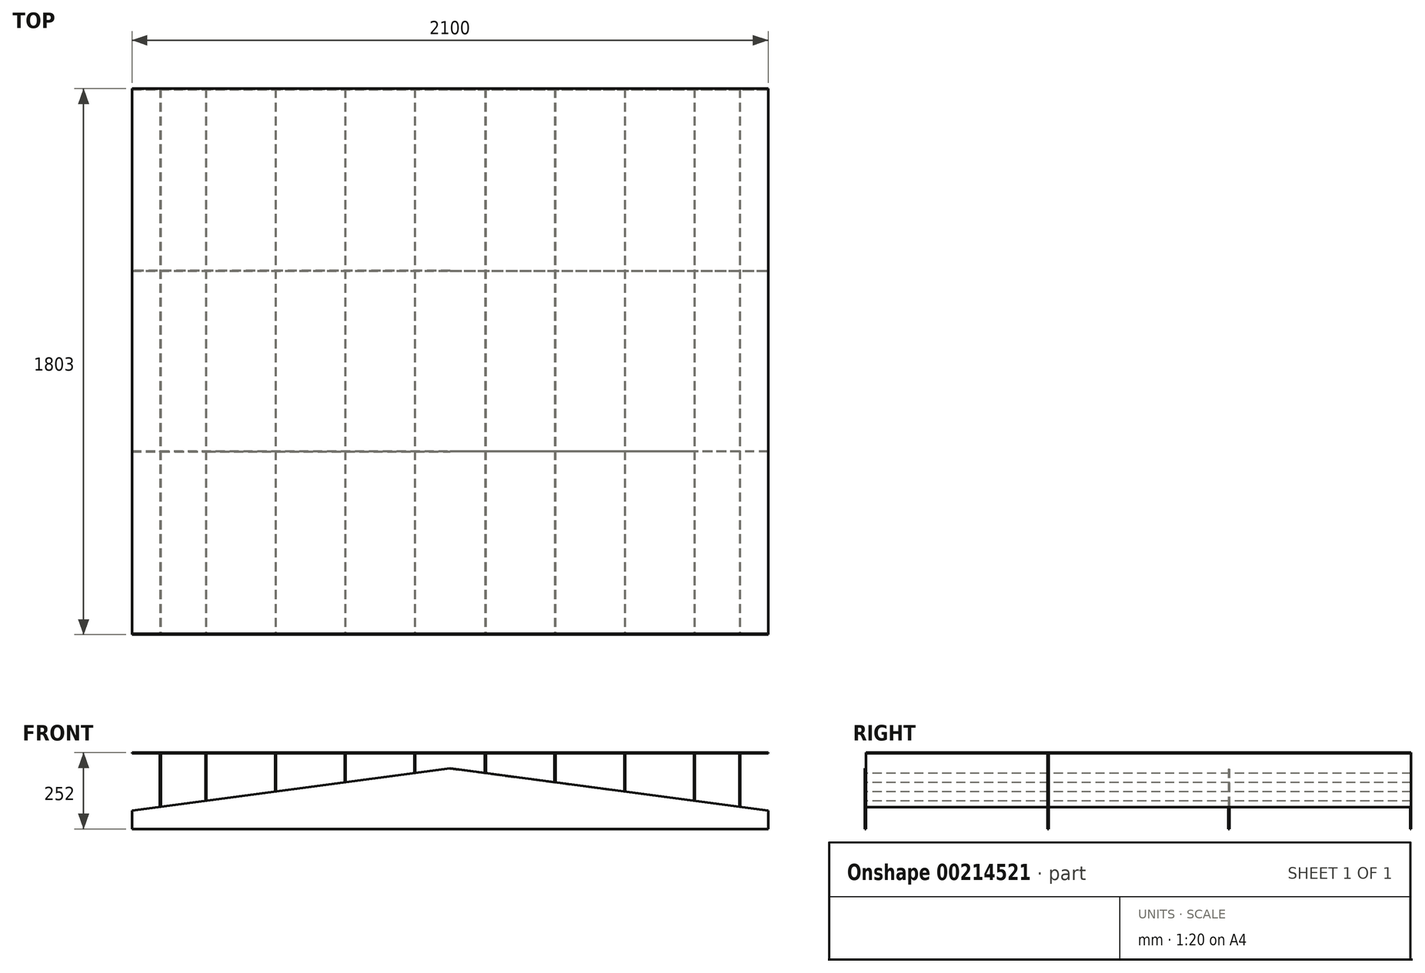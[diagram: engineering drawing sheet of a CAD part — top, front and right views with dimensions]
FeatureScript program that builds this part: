
annotation { "Feature Type Name" : "Feature", "Feature Type Description" : "" }
export const myFeature = defineFeature(function(context is Context, id is Id, definition is map)
    precondition{}
    {
        {
            var Q0;
            Q0=qCreatedBy(makeId("Front.planeOp"),FACE);
            var sketch = newSketch(context, id + "F0", { "sketchPlane" : qUnion([Q0])});
            skLineSegment(sketch, "E0", {"start": v(0, -314.94) * mm, "end": v(-1050, -314.94) * mm});
            skLineSegment(sketch, "E1", {"start": v(-1050, -314.94) * mm, "end": v(-1050, -254.94) * mm});
            skLineSegment(sketch, "E2", {"start": v(-1050, -254.94) * mm, "end": v(0, -114.94) * mm});
            skLineSegment(sketch, "E3", {"start": v(0, -64.94) * mm, "end": v(-1050, -64.94) * mm, "construction": true});
            skLineSegment(sketch, "E4.bottom", {"start": v(-118, -64.94) * mm, "end": v(-115, -64.94) * mm});
            skLineSegment(sketch, "E4.top", {"start": v(-118, -130.67) * mm, "end": v(-115, -130.27) * mm});
            skLineSegment(sketch, "E4.left", {"start": v(-118, -64.94) * mm, "end": v(-118, -130.67) * mm});
            skLineSegment(sketch, "E4.right", {"start": v(-115, -64.94) * mm, "end": v(-115, -130.27) * mm});
            skLineSegment(sketch, "E5.bottom", {"start": v(-348, -64.94) * mm, "end": v(-345, -64.94) * mm});
            skLineSegment(sketch, "E5.top", {"start": v(-348, -161.34) * mm, "end": v(-345, -160.94) * mm});
            skLineSegment(sketch, "E5.left", {"start": v(-348, -64.94) * mm, "end": v(-348, -161.34) * mm});
            skLineSegment(sketch, "E5.right", {"start": v(-345, -64.94) * mm, "end": v(-345, -160.94) * mm});
            skLineSegment(sketch, "E6.bottom", {"start": v(-578, -64.94) * mm, "end": v(-575, -64.94) * mm});
            skLineSegment(sketch, "E6.top", {"start": v(-578, -192) * mm, "end": v(-575, -191.6) * mm});
            skLineSegment(sketch, "E6.left", {"start": v(-578, -64.94) * mm, "end": v(-578, -192) * mm});
            skLineSegment(sketch, "E6.right", {"start": v(-575, -64.94) * mm, "end": v(-575, -191.6) * mm});
            skLineSegment(sketch, "E7.bottom", {"start": v(-808, -64.94) * mm, "end": v(-805, -64.94) * mm});
            skLineSegment(sketch, "E7.top", {"start": v(-808, -222.67) * mm, "end": v(-805, -222.27) * mm});
            skLineSegment(sketch, "E7.left", {"start": v(-808, -64.94) * mm, "end": v(-808, -222.67) * mm});
            skLineSegment(sketch, "E7.right", {"start": v(-805, -64.94) * mm, "end": v(-805, -222.27) * mm});
            skLineSegment(sketch, "E8.bottom", {"start": v(-958, -64.94) * mm, "end": v(-955, -64.94) * mm});
            skLineSegment(sketch, "E8.top", {"start": v(-958, -242.67) * mm, "end": v(-955, -242.27) * mm});
            skLineSegment(sketch, "E8.left", {"start": v(-958, -64.94) * mm, "end": v(-958, -242.67) * mm});
            skLineSegment(sketch, "E8.right", {"start": v(-955, -64.94) * mm, "end": v(-955, -242.27) * mm});
            skLineSegment(sketch, "E9.MirrorCS", {"start": v(578, -192) * mm, "end": v(575, -191.6) * mm});
            skLineSegment(sketch, "E10.MirrorCS", {"start": v(958, -242.67) * mm, "end": v(955, -242.27) * mm});
            skLineSegment(sketch, "E11.MirrorCS", {"start": v(578, -64.94) * mm, "end": v(575, -64.94) * mm});
            skLineSegment(sketch, "E12.MirrorCS", {"start": v(348, -161.34) * mm, "end": v(345, -160.94) * mm});
            skLineSegment(sketch, "E13.MirrorCS", {"start": v(808, -222.67) * mm, "end": v(805, -222.27) * mm});
            skLineSegment(sketch, "E14.MirrorCS", {"start": v(348, -64.94) * mm, "end": v(345, -64.94) * mm});
            skLineSegment(sketch, "E15.MirrorCS", {"start": v(958, -64.94) * mm, "end": v(955, -64.94) * mm});
            skLineSegment(sketch, "E16.MirrorCS", {"start": v(808, -64.94) * mm, "end": v(805, -64.94) * mm});
            skLineSegment(sketch, "E17.MirrorCS", {"start": v(118, -64.94) * mm, "end": v(115, -64.94) * mm});
            skLineSegment(sketch, "E18.MirrorCS", {"start": v(118, -130.67) * mm, "end": v(115, -130.27) * mm});
            skLineSegment(sketch, "E19.MirrorCS", {"start": v(575, -64.94) * mm, "end": v(575, -191.6) * mm});
            skLineSegment(sketch, "E20.MirrorCS", {"start": v(118, -64.94) * mm, "end": v(118, -130.67) * mm});
            skLineSegment(sketch, "E21.MirrorCS", {"start": v(1050, -314.94) * mm, "end": v(1050, -254.94) * mm});
            skLineSegment(sketch, "E22.MirrorCS", {"start": v(115, -64.94) * mm, "end": v(115, -130.27) * mm});
            skLineSegment(sketch, "E23.MirrorCS", {"start": v(955, -64.94) * mm, "end": v(955, -242.27) * mm});
            skLineSegment(sketch, "E24.MirrorCS", {"start": v(805, -64.94) * mm, "end": v(805, -222.27) * mm});
            skLineSegment(sketch, "E25.MirrorCS", {"start": v(348, -64.94) * mm, "end": v(348, -161.34) * mm});
            skLineSegment(sketch, "E26.MirrorCS", {"start": v(578, -64.94) * mm, "end": v(578, -192) * mm});
            skLineSegment(sketch, "E27.MirrorCS", {"start": v(958, -64.94) * mm, "end": v(958, -242.67) * mm});
            skLineSegment(sketch, "E28.MirrorCS", {"start": v(345, -64.94) * mm, "end": v(345, -160.94) * mm});
            skLineSegment(sketch, "E29.MirrorCS", {"start": v(1050, -254.94) * mm, "end": v(0, -114.94) * mm});
            skLineSegment(sketch, "E30.MirrorCS", {"start": v(0, -314.94) * mm, "end": v(1050, -314.94) * mm});
            skLineSegment(sketch, "E31.MirrorCS", {"start": v(808, -64.94) * mm, "end": v(808, -222.67) * mm});
            skLineSegment(sketch, "E32.MirrorCS", {"start": v(0, -64.94) * mm, "end": v(1050, -64.94) * mm, "construction": true});
            skSolve(sketch);
        }
        {
            var Q0;
            Q0 = qSketchRegion(id + "F0", true);
            extrude(context, id + "F1", {"entities" : qUnion([Q0]), "depth" : 3 * mm, "offsetDistance" : 25 * mm});
        }
        {
            var Q0;
            Q0=makeQuery(id+"F1.opExtrude","CAP_FACE",FACE,{"disambiguationData":[OSD([sQuery(id+"F0.wireOp",EDGE,"E0"),sQuery(id+"F0.wireOp",EDGE,"E1"),sQuery(id+"F0.wireOp",EDGE,"E2"),sQuery(id+"F0.wireOp",EDGE,"E4.bottom"),sQuery(id+"F0.wireOp",EDGE,"E4.left"),sQuery(id+"F0.wireOp",EDGE,"E4.right"),sQuery(id+"F0.wireOp",EDGE,"E5.bottom"),sQuery(id+"F0.wireOp",EDGE,"E5.left"),sQuery(id+"F0.wireOp",EDGE,"E5.right"),sQuery(id+"F0.wireOp",EDGE,"E6.bottom"),sQuery(id+"F0.wireOp",EDGE,"E6.left"),sQuery(id+"F0.wireOp",EDGE,"E6.right"),sQuery(id+"F0.wireOp",EDGE,"E7.bottom"),sQuery(id+"F0.wireOp",EDGE,"E7.left"),sQuery(id+"F0.wireOp",EDGE,"E7.right"),sQuery(id+"F0.wireOp",EDGE,"E8.bottom"),sQuery(id+"F0.wireOp",EDGE,"E8.left"),sQuery(id+"F0.wireOp",EDGE,"E8.right"),sQuery(id+"F0.wireOp",EDGE,"E11.MirrorCS"),sQuery(id+"F0.wireOp",EDGE,"E14.MirrorCS"),sQuery(id+"F0.wireOp",EDGE,"E15.MirrorCS"),sQuery(id+"F0.wireOp",EDGE,"E16.MirrorCS"),sQuery(id+"F0.wireOp",EDGE,"E17.MirrorCS"),sQuery(id+"F0.wireOp",EDGE,"E19.MirrorCS"),sQuery(id+"F0.wireOp",EDGE,"E20.MirrorCS"),sQuery(id+"F0.wireOp",EDGE,"E21.MirrorCS"),sQuery(id+"F0.wireOp",EDGE,"E22.MirrorCS"),sQuery(id+"F0.wireOp",EDGE,"E23.MirrorCS"),sQuery(id+"F0.wireOp",EDGE,"E24.MirrorCS"),sQuery(id+"F0.wireOp",EDGE,"E25.MirrorCS"),sQuery(id+"F0.wireOp",EDGE,"E26.MirrorCS"),sQuery(id+"F0.wireOp",EDGE,"E27.MirrorCS"),sQuery(id+"F0.wireOp",EDGE,"E28.MirrorCS"),sQuery(id+"F0.wireOp",EDGE,"E29.MirrorCS"),sQuery(id+"F0.wireOp",EDGE,"E30.MirrorCS"),sQuery(id+"F0.wireOp",EDGE,"E31.MirrorCS")])],"isStart":false});
            cPlane(context, id + "F2", {"entities" : qUnion([Q0]), "cplaneType" : CPlaneType.OFFSET, "offset" : 600 * mm, "width" : 150 * mm, "height" : 150 * mm});
        }
        {
            var Q0;
            Q0=qCreatedBy(id+"F2.planeOp",FACE);
            var sketch = newSketch(context, id + "F3", { "sketchPlane" : qUnion([Q0])});
            skLineSegment(sketch, "E33.bottom", {"start": v(-958, -64.94) * mm, "end": v(-955, -64.94) * mm});
            skLineSegment(sketch, "E33.top", {"start": v(-958, -242.67) * mm, "end": v(-955, -242.67) * mm});
            skLineSegment(sketch, "E33.left", {"start": v(-958, -64.94) * mm, "end": v(-958, -242.67) * mm});
            skLineSegment(sketch, "E33.right", {"start": v(-955, -64.94) * mm, "end": v(-955, -242.67) * mm});
            skLineSegment(sketch, "E34.bottom", {"start": v(-808, -64.94) * mm, "end": v(-805, -64.94) * mm});
            skLineSegment(sketch, "E34.top", {"start": v(-808, -222.67) * mm, "end": v(-805, -222.67) * mm});
            skLineSegment(sketch, "E34.left", {"start": v(-808, -64.94) * mm, "end": v(-808, -222.67) * mm});
            skLineSegment(sketch, "E34.right", {"start": v(-805, -64.94) * mm, "end": v(-805, -222.67) * mm});
            skLineSegment(sketch, "E35.bottom", {"start": v(-578, -64.94) * mm, "end": v(-575, -64.94) * mm});
            skLineSegment(sketch, "E35.top", {"start": v(-578, -192) * mm, "end": v(-575, -192) * mm});
            skLineSegment(sketch, "E35.left", {"start": v(-578, -64.94) * mm, "end": v(-578, -192) * mm});
            skLineSegment(sketch, "E35.right", {"start": v(-575, -64.94) * mm, "end": v(-575, -192) * mm});
            skLineSegment(sketch, "E36.bottom", {"start": v(-348, -64.94) * mm, "end": v(-345, -64.94) * mm});
            skLineSegment(sketch, "E36.top", {"start": v(-348, -161.34) * mm, "end": v(-345, -161.34) * mm});
            skLineSegment(sketch, "E36.left", {"start": v(-348, -64.94) * mm, "end": v(-348, -161.34) * mm});
            skLineSegment(sketch, "E36.right", {"start": v(-345, -64.94) * mm, "end": v(-345, -161.34) * mm});
            skLineSegment(sketch, "E37.bottom", {"start": v(-118, -64.94) * mm, "end": v(-115, -64.94) * mm});
            skLineSegment(sketch, "E37.top", {"start": v(-118, -130.67) * mm, "end": v(-115, -130.67) * mm});
            skLineSegment(sketch, "E37.left", {"start": v(-118, -64.94) * mm, "end": v(-118, -130.67) * mm});
            skLineSegment(sketch, "E37.right", {"start": v(-115, -64.94) * mm, "end": v(-115, -130.67) * mm});
            skLineSegment(sketch, "E38.MirrorCS", {"start": v(348, -161.34) * mm, "end": v(345, -161.34) * mm});
            skLineSegment(sketch, "E39.MirrorCS", {"start": v(578, -64.94) * mm, "end": v(575, -64.94) * mm});
            skLineSegment(sketch, "E40.MirrorCS", {"start": v(808, -222.67) * mm, "end": v(805, -222.67) * mm});
            skLineSegment(sketch, "E41.MirrorCS", {"start": v(348, -64.94) * mm, "end": v(345, -64.94) * mm});
            skLineSegment(sketch, "E42.MirrorCS", {"start": v(118, -130.67) * mm, "end": v(115, -130.67) * mm});
            skLineSegment(sketch, "E43.MirrorCS", {"start": v(958, -64.94) * mm, "end": v(955, -64.94) * mm});
            skLineSegment(sketch, "E44.MirrorCS", {"start": v(115, -64.94) * mm, "end": v(115, -130.67) * mm});
            skLineSegment(sketch, "E45.MirrorCS", {"start": v(958, -242.67) * mm, "end": v(955, -242.67) * mm});
            skLineSegment(sketch, "E46.MirrorCS", {"start": v(118, -64.94) * mm, "end": v(118, -130.67) * mm});
            skLineSegment(sketch, "E47.MirrorCS", {"start": v(578, -192) * mm, "end": v(575, -192) * mm});
            skLineSegment(sketch, "E48.MirrorCS", {"start": v(808, -64.94) * mm, "end": v(805, -64.94) * mm});
            skLineSegment(sketch, "E49.MirrorCS", {"start": v(118, -64.94) * mm, "end": v(115, -64.94) * mm});
            skLineSegment(sketch, "E50.MirrorCS", {"start": v(575, -64.94) * mm, "end": v(575, -192) * mm});
            skLineSegment(sketch, "E51.MirrorCS", {"start": v(958, -64.94) * mm, "end": v(958, -242.67) * mm});
            skLineSegment(sketch, "E52.MirrorCS", {"start": v(348, -64.94) * mm, "end": v(348, -161.34) * mm});
            skLineSegment(sketch, "E53.MirrorCS", {"start": v(955, -64.94) * mm, "end": v(955, -242.67) * mm});
            skLineSegment(sketch, "E54.MirrorCS", {"start": v(805, -64.94) * mm, "end": v(805, -222.67) * mm});
            skLineSegment(sketch, "E55.MirrorCS", {"start": v(808, -64.94) * mm, "end": v(808, -222.67) * mm});
            skLineSegment(sketch, "E56.MirrorCS", {"start": v(345, -64.94) * mm, "end": v(345, -161.34) * mm});
            skLineSegment(sketch, "E57.MirrorCS", {"start": v(578, -64.94) * mm, "end": v(578, -192) * mm});
            skSolve(sketch);
        }
        {
            var Q0;
            Q0 = qSketchRegion(id + "F3", true);
            extrude(context, id + "F4", {"entities" : qUnion([Q0]), "oppositeDirection" : true, "depth" : 1800 * mm, "offsetDistance" : 25 * mm});
        }
        {
            var Q0;
            Q0=qCreatedBy(id+"F2.planeOp",FACE);
            cPlane(context, id + "F5", {"entities" : qUnion([Q0]), "cplaneType" : CPlaneType.OFFSET, "offset" : 1200 * mm, "oppositeDirection" : true, "width" : 150 * mm, "height" : 150 * mm});
        }
        {
            var Q0;
            Q0=qCreatedBy(id+"F5.planeOp",FACE);
            var sketch = newSketch(context, id + "F6", { "sketchPlane" : qUnion([Q0])});
            skLineSegment(sketch, "E58", {"start": v(0, -116.92) * mm, "end": v(-1050, -254.94) * mm});
            skLineSegment(sketch, "E59", {"start": v(-1050, -254.94) * mm, "end": v(-1050, -314.94) * mm});
            skLineSegment(sketch, "E60", {"start": v(-1050, -314.94) * mm, "end": v(0, -314.94) * mm});
            skLineSegment(sketch, "E61.MirrorCS", {"start": v(1050, -254.94) * mm, "end": v(1050, -314.94) * mm});
            skLineSegment(sketch, "E62.MirrorCS", {"start": v(0, -116.92) * mm, "end": v(1050, -254.94) * mm});
            skLineSegment(sketch, "E63.MirrorCS", {"start": v(1050, -314.94) * mm, "end": v(0, -314.94) * mm});
            skSolve(sketch);
        }
        {
            var Q0;
            Q0 = qSketchRegion(id + "F6", true);
            extrude(context, id + "F7", {"entities" : qUnion([Q0]), "depth" : 3 * mm, "offsetDistance" : 25 * mm});
        }
        {
            var Q0;
            Q0=qCreatedBy(id+"F5.planeOp",FACE);
            cPlane(context, id + "F8", {"entities" : qUnion([Q0]), "cplaneType" : CPlaneType.OFFSET, "offset" : 600 * mm, "oppositeDirection" : true, "width" : 150 * mm, "height" : 150 * mm});
        }
        {
            var Q0;
            Q0=qCreatedBy(id+"F8.planeOp",FACE);
            var sketch = newSketch(context, id + "F9", { "sketchPlane" : qUnion([Q0])});
            skLineSegment(sketch, "E64", {"start": v(0, -114.94) * mm, "end": v(-1050, -254.94) * mm});
            skLineSegment(sketch, "E65", {"start": v(-1050, -254.94) * mm, "end": v(-1050, -314.94) * mm});
            skLineSegment(sketch, "E66", {"start": v(-1050, -314.94) * mm, "end": v(0, -314.94) * mm});
            skLineSegment(sketch, "E67.MirrorCS", {"start": v(1050, -254.94) * mm, "end": v(1050, -314.94) * mm});
            skLineSegment(sketch, "E68.MirrorCS", {"start": v(1050, -314.94) * mm, "end": v(0, -314.94) * mm});
            skLineSegment(sketch, "E69.MirrorCS", {"start": v(0, -114.94) * mm, "end": v(1050, -254.94) * mm});
            skSolve(sketch);
        }
        {
            var Q0;
            Q0 = qSketchRegion(id + "F9", true);
            extrude(context, id + "F10", {"entities" : qUnion([Q0]), "depth" : 3 * mm, "offsetDistance" : 25 * mm});
        }
        {
            var Q0;
            Q0=makeQuery(id+"F4.opExtrude","SWEPT_FACE",FACE,{"disambiguationData":[OSD([sQuery(id+"F3.wireOp",EDGE,"E33.bottom")])]});
            var sketch = newSketch(context, id + "F11", { "sketchPlane" : qUnion([Q0])});
            skLineSegment(sketch, "E70.bottom", {"start": v(-1050, 1197) * mm, "end": v(1050, 1197) * mm});
            skLineSegment(sketch, "E70.top", {"start": v(-1050, -603) * mm, "end": v(1050, -603) * mm});
            skLineSegment(sketch, "E70.left", {"start": v(-1050, 1197) * mm, "end": v(-1050, -603) * mm});
            skLineSegment(sketch, "E70.right", {"start": v(1050, 1197) * mm, "end": v(1050, -603) * mm});
            skSolve(sketch);
        }
        {
            var Q0;
            Q0 = qSketchRegion(id + "F11", true);
            extrude(context, id + "F12", {"entities" : qUnion([Q0]), "depth" : 2 * mm, "offsetDistance" : 25 * mm});
        }
        {
            var Q0;
            Q0=qCreatedBy(id+"F2.planeOp",FACE);
            var sketch = newSketch(context, id + "F13", { "sketchPlane" : qUnion([Q0])});
            skLineSegment(sketch, "E71", {"start": v(0, -114.94) * mm, "end": v(-1050, -254.94) * mm});
            skLineSegment(sketch, "E72", {"start": v(-1050, -254.94) * mm, "end": v(-1050, -314.94) * mm});
            skLineSegment(sketch, "E73", {"start": v(-1050, -314.94) * mm, "end": v(0, -314.94) * mm});
            skLineSegment(sketch, "E74.MirrorCS", {"start": v(0, -114.94) * mm, "end": v(1050, -254.94) * mm});
            skLineSegment(sketch, "E75.MirrorCS", {"start": v(1050, -314.94) * mm, "end": v(0, -314.94) * mm});
            skLineSegment(sketch, "E76.MirrorCS", {"start": v(1050, -254.94) * mm, "end": v(1050, -314.94) * mm});
            skSolve(sketch);
        }
        {
            var Q0;
            Q0 = qSketchRegion(id + "F13", true);
            extrude(context, id + "F14", {"entities" : qUnion([Q0]), "depth" : 3 * mm, "offsetDistance" : 25 * mm});
        }
    });
